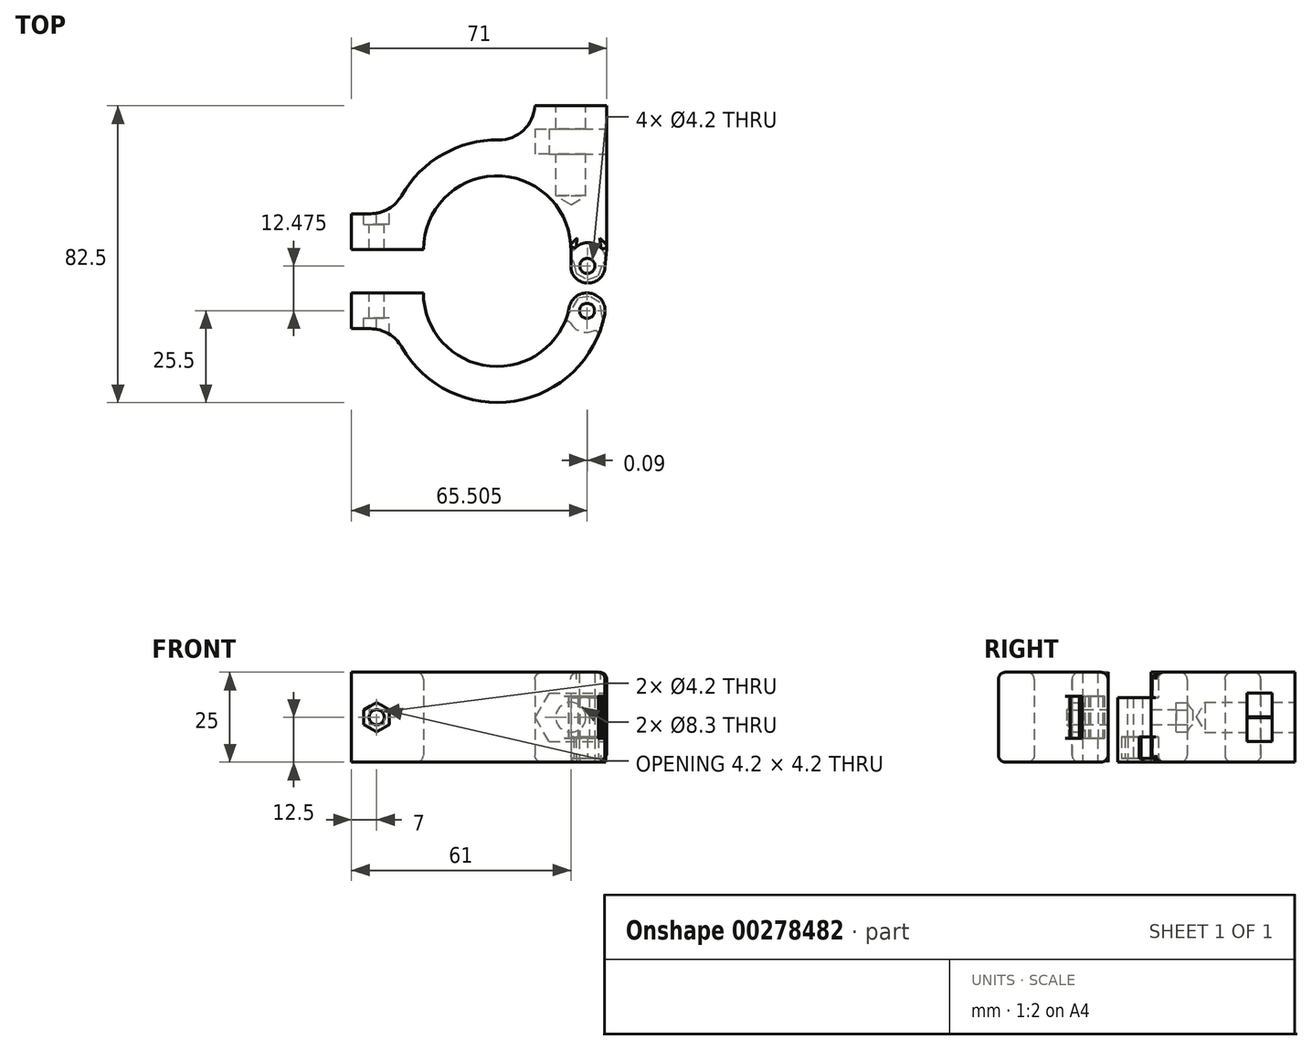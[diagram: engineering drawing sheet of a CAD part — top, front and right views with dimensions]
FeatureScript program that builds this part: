
annotation { "Feature Type Name" : "Feature", "Feature Type Description" : "" }
export const myFeature = defineFeature(function(context is Context, id is Id, definition is map)
    precondition{}
    {
        {
            var Q0;
            Q0=qCreatedBy(makeId("Top.planeOp"),FACE);
            var sketch = newSketch(context, id + "F0", { "sketchPlane" : qUnion([Q0])});
            skArc(sketch, "E0", {"start": v(20.5, 0) * mm, "mid": v(0, 20.5) * mm, "end": v(-20.5, 0) * mm});
            skArc(sketch, "E1", {"start": v(-28.81, 10) * mm, "mid": v(5.07, 30.08) * mm, "end": v(30.5, 0) * mm});
            skLineSegment(sketch, "E2", {"start": v(-30.5, 0) * mm, "end": v(-20.5, 0) * mm});
            skLineSegment(sketch, "E3", {"start": v(20.5, 0) * mm, "end": v(20.5, -5) * mm});
            skLineSegment(sketch, "E4", {"start": v(30, -5) * mm, "end": v(30.5, 0) * mm});
            skPoint(sketch, "E5", {"position": v(0, -12) * mm});
            skArc(sketch, "E6", {"start": v(20.5, -5) * mm, "mid": v(25.25, -9.3) * mm, "end": v(30, -5) * mm});
            skArc(sketch, "E7", {"start": v(-20.5, -12) * mm, "mid": v(-2.02, -32.4) * mm, "end": v(20.1, -16.02) * mm});
            skArc(sketch, "E8", {"start": v(-28.81, -22) * mm, "mid": v(2.08, -42.43) * mm, "end": v(29.9, -17.98) * mm});
            skLineSegment(sketch, "E9", {"start": v(25, -12) * mm, "end": v(25, -12) * mm});
            skLineSegment(sketch, "E10", {"start": v(-20.5, -12) * mm, "end": v(-30.5, -12) * mm});
            skPoint(sketch, "E11.visualSharp", {"position": v(20.5, -12) * mm});
            skArc(sketch, "E11.filletArc", {"start": v(25, -12) * mm, "mid": v(21.83, -13.13) * mm, "end": v(20.1, -16.02) * mm});
            skPoint(sketch, "E12.visualSharp", {"position": v(30.5, -12) * mm});
            skArc(sketch, "E12.filletArc", {"start": v(29.9, -17.98) * mm, "mid": v(28.87, -13.83) * mm, "end": v(25, -12) * mm});
            skCircle(sketch, "E13", {"center": v(25, -17) * mm, "radius": 2.1 * mm});
            skArc(sketch, "E14", {"start": v(19.88, -17.02) * mm, "mid": v(23.81, -22.9) * mm, "end": v(29.7, -18.96) * mm});
            skPoint(sketch, "E15", {"position": v(-25.5, 0) * mm});
            skArc(sketch, "E16", {"start": v(19.74, -16.14) * mm, "mid": v(-19.53, 16.4) * mm, "end": v(19.32, -16.65) * mm, "construction": true});
            skCircle(sketch, "E17", {"center": v(25.1, -4.52) * mm, "radius": 2.1 * mm});
            skArc(sketch, "E18", {"start": v(30.25, -2.5) * mm, "mid": v(25.64, 1.95) * mm, "end": v(20.5, -1.88) * mm});
            skLineSegment(sketch, "E19", {"start": v(-30.5, 0) * mm, "end": v(-40.5, 0) * mm});
            skLineSegment(sketch, "E20", {"start": v(-40.5, 0) * mm, "end": v(-40.5, 10) * mm});
            skLineSegment(sketch, "E21", {"start": v(-40.5, 10) * mm, "end": v(-28.81, 10) * mm});
            skLineSegment(sketch, "E22", {"start": v(-30.5, -12) * mm, "end": v(-40.5, -12) * mm});
            skLineSegment(sketch, "E23", {"start": v(-40.5, -12) * mm, "end": v(-40.5, -22) * mm});
            skLineSegment(sketch, "E24", {"start": v(-40.5, -22) * mm, "end": v(-28.81, -22) * mm});
            skLineSegment(sketch, "E25", {"start": v(30.5, 0) * mm, "end": v(30.5, 40) * mm});
            skLineSegment(sketch, "E26", {"start": v(30.5, 40) * mm, "end": v(10.5, 40) * mm});
            skLineSegment(sketch, "E27", {"start": v(10.5, 40) * mm, "end": v(10.5, 17.6) * mm});
            skArc(sketch, "E28", {"start": v(29.13, -18.41) * mm, "mid": v(29.22, -18.91) * mm, "end": v(29.64, -19.2) * mm});
            skArc(sketch, "E29", {"start": v(19.79, -17.36) * mm, "mid": v(20.27, -17.28) * mm, "end": v(20.56, -16.89) * mm});
            skArc(sketch, "E30", {"start": v(30.16, -3.4) * mm, "mid": v(29.76, -3.5) * mm, "end": v(29.5, -3.8) * mm});
            skArc(sketch, "E31", {"start": v(21.32, -3.62) * mm, "mid": v(21.08, -3.03) * mm, "end": v(20.5, -2.8) * mm});
            skLineSegment(sketch, "E32", {"start": v(21.92, -6.53) * mm, "end": v(25.16, -8.35) * mm});
            skLineSegment(sketch, "E33", {"start": v(25.16, -8.35) * mm, "end": v(28.18, -7.26) * mm});
            skLineSegment(sketch, "E34", {"start": v(28.18, -7.26) * mm, "end": v(29.5, -3.8) * mm});
            skPoint(sketch, "E35.center.orphan", {"position": v(25.25, -9.3) * mm});
            skPoint(sketch, "E36.start.orphan", {"position": v(21.32, -3.62) * mm});
            skLineSegment(sketch, "E37", {"start": v(21.32, -3.62) * mm, "end": v(21.92, -6.53) * mm});
            skLineSegment(sketch, "E38", {"start": v(20.56, -16.89) * mm, "end": v(22.42, -13.53) * mm});
            skLineSegment(sketch, "E39", {"start": v(22.42, -13.53) * mm, "end": v(25.66, -13.05) * mm});
            skPoint(sketch, "E39.endSnap0", {"position": v(25.66, -13) * mm});
            skLineSegment(sketch, "E40", {"start": v(25.66, -13.05) * mm, "end": v(28.58, -14.72) * mm});
            skLineSegment(sketch, "E41", {"start": v(28.58, -14.72) * mm, "end": v(29.13, -18.41) * mm});
            skSolve(sketch);
        }
        {
            var Q0;
            {var subQ1=sQuery(id+"F0.wireOp",EDGE,"E0");Q0=makeQuery(id+"F0.imprint","IMPRINT",FACE,{"disambiguationData":[TD([[makeQuery(id+"F0.imprint","IMPRINT",EDGE,{"derivedFrom":subQ1}),-1.0]])]});}
            var Q1;
            {var subQ6=sQuery(id+"F0.wireOp",EDGE,"E10");Q1=makeQuery(id+"F0.imprint","IMPRINT",FACE,{"disambiguationData":[TD([[makeQuery(id+"F0.imprint","IMPRINT",EDGE,{"derivedFrom":subQ6}),1.0]])]});}
            var Q2;
            {var subQ0=sQuery(id+"F0.wireOp",EDGE,"E25");Q2=makeQuery(id+"F0.imprint","IMPRINT",FACE,{"disambiguationData":[TD([[makeQuery(id+"F0.imprint","IMPRINT",EDGE,{"derivedFrom":subQ0}),1.0]])]});}
            var Q3;
            {var subQ0=sQuery(id+"F0.wireOp",EDGE,"E2");Q3=makeQuery(id+"F0.imprint","IMPRINT",FACE,{"disambiguationData":[TD([[makeQuery(id+"F0.imprint","IMPRINT",EDGE,{"derivedFrom":subQ0}),1.0]])]});}
            var Q4;
            {var subQ0=sQuery(id+"F0.wireOp",EDGE,"E14");var subQ1=sQuery(id+"F0.wireOp",EDGE,"E7");var subQ2=makeQuery(id+"F0.imprint","INTERSECT",VERTEX,{"derivedFrom":[subQ1,subQ0]});Q4=makeQuery(id+"F0.imprint","IMPRINT",FACE,{"disambiguationData":[TD([[makeQuery(id+"F0.imprint","IMPRINT",EDGE,{"disambiguationData":[TD([[subQ2,1.0]])],"derivedFrom":subQ1}),-1.0]])]});}
            extrude(context, id + "F1", {"entities" : qUnion([Q0, Q1, Q2, Q3, Q4]), "depth" : 25 * mm});
        }
        {
            var Q0;
            {var subQ0=sQuery(id+"F0.wireOp",EDGE,"E6");Q0=makeQuery(id+"F0.imprint","IMPRINT",FACE,{"disambiguationData":[TD([[makeQuery(id+"F0.imprint","IMPRINT",EDGE,{"derivedFrom":subQ0}),1.0]])]});}
            var Q1;
            {var subQ0=sQuery(id+"F0.wireOp",EDGE,"E35");var subQ1=sQuery(id+"F0.wireOp",EDGE,"E6");var subQ2=makeQuery(id+"F0.imprint","INTERSECT",VERTEX,{"disambiguationData":[OD(0.0)],"derivedFrom":[subQ1,subQ0]});Q1=makeQuery(id+"F0.imprint","IMPRINT",FACE,{"disambiguationData":[TD([[makeQuery(id+"F0.imprint","IMPRINT",EDGE,{"disambiguationData":[TD([[subQ2,-1.0]])],"derivedFrom":subQ1}),1.0]])]});}
            var Q2;
            {var subQ0=sQuery(id+"F0.wireOp",EDGE,"jxJWhOyt-H9XI-TiTa-gCL7-cOyN3CCPrfDy");var subQ1=sQuery(id+"F0.wireOp",EDGE,"E6");var subQ2=makeQuery(id+"F0.imprint","INTERSECT",VERTEX,{"disambiguationData":[OD(0.0)],"derivedFrom":[subQ1,subQ0]});Q2=makeQuery(id+"F0.imprint","IMPRINT",FACE,{"disambiguationData":[TD([[makeQuery(id+"F0.imprint","IMPRINT",EDGE,{"disambiguationData":[TD([[subQ2,-1.0]])],"derivedFrom":subQ1}),1.0]])]});}
            var Q3;
            {var subQ0=sQuery(id+"F0.wireOp",EDGE,"8LRzmeCb-BIhQ-DYdr-IcR4-9TPCuBTbz9Ep");var subQ1=sQuery(id+"F0.wireOp",EDGE,"E6");var subQ2=makeQuery(id+"F0.imprint","INTERSECT",VERTEX,{"disambiguationData":[OD(0.0)],"derivedFrom":[subQ1,subQ0]});Q3=makeQuery(id+"F0.imprint","IMPRINT",FACE,{"disambiguationData":[TD([[makeQuery(id+"F0.imprint","IMPRINT",EDGE,{"disambiguationData":[TD([[subQ2,-1.0]])],"derivedFrom":subQ1}),1.0]])]});}
            var Q4;
            {var subQ0=sQuery(id+"F0.wireOp",EDGE,"E31");var subQ1=sQuery(id+"F0.wireOp",EDGE,"E3");var subQ2=makeQuery(id+"F0.imprint","INTERSECT",VERTEX,{"disambiguationData":[OD(0.0)],"derivedFrom":[subQ1,subQ0]});Q4=makeQuery(id+"F0.imprint","IMPRINT",FACE,{"disambiguationData":[TD([[makeQuery(id+"F0.imprint","IMPRINT",EDGE,{"disambiguationData":[TD([[subQ2,-1.0]])],"derivedFrom":subQ1}),1.0]])]});}
            var Q5;
            {var subQ0=sQuery(id+"F0.wireOp",EDGE,"E30");var subQ1=sQuery(id+"F0.wireOp",EDGE,"E4");var subQ2=makeQuery(id+"F0.imprint","INTERSECT",VERTEX,{"disambiguationData":[OD(0.0)],"derivedFrom":[subQ1,subQ0]});Q5=makeQuery(id+"F0.imprint","IMPRINT",FACE,{"disambiguationData":[TD([[makeQuery(id+"F0.imprint","IMPRINT",EDGE,{"disambiguationData":[TD([[subQ2,-1.0]])],"derivedFrom":subQ1}),1.0]])]});}
            extrude(context, id + "F2", {"entities" : qUnion([Q0, Q1, Q2, Q3, Q4, Q5]), "operationType" : NewBodyOperationType.ADD, "depth" : 18 * mm, "hasSecondDirection" : true, "secondDirectionOppositeDirection" : false, "secondDirectionDepth" : 7 * mm});
        }
        {
            var Q0;
            {var subQ5=sQuery(id+"F0.wireOp",EDGE,"E11.filletArc");Q0=makeQuery(id+"F0.imprint","IMPRINT",FACE,{"disambiguationData":[TD([[makeQuery(id+"F0.imprint","IMPRINT",EDGE,{"derivedFrom":subQ5}),1.0]])]});}
            var Q1;
            Q1=makeQuery(id+"F0.imprint","IMPRINT",FACE,{"disambiguationData":[TD([[makeQuery(id+"F0.imprint","IMPRINT",EDGE,{"derivedFrom":sQuery(id+"F0.wireOp",EDGE,"E13")}),-1.0]])]});
            var Q2;
            {var subQ0=sQuery(id+"F0.wireOp",EDGE,"E12.filletArc");var subQ1=sQuery(id+"F0.wireOp",EDGE,"E11.filletArc");var subQ2=makeQuery(id+"F0.imprint","INTERSECT",VERTEX,{"derivedFrom":[subQ1,subQ0]});Q2=makeQuery(id+"F0.imprint","IMPRINT",FACE,{"disambiguationData":[TD([[makeQuery(id+"F0.imprint","IMPRINT",EDGE,{"disambiguationData":[TD([[subQ2,-1.0]])],"derivedFrom":subQ1}),1.0]])]});}
            var Q3;
            {var subQ0=sQuery(id+"F0.wireOp",EDGE,"uIjLM5ln-C2pQ-Ehxs-1cjr-M9Mzx9JWShuk");var subQ1=sQuery(id+"F0.wireOp",EDGE,"E12.filletArc");var subQ2=makeQuery(id+"F0.imprint","INTERSECT",VERTEX,{"disambiguationData":[OD(0.0)],"derivedFrom":[subQ1,subQ0]});Q3=makeQuery(id+"F0.imprint","IMPRINT",FACE,{"disambiguationData":[TD([[makeQuery(id+"F0.imprint","IMPRINT",EDGE,{"disambiguationData":[TD([[subQ2,-1.0]])],"derivedFrom":subQ1}),1.0]])]});}
            var Q4;
            {var subQ0=sQuery(id+"F0.wireOp",EDGE,"E14");var subQ1=sQuery(id+"F0.wireOp",EDGE,"E7");var subQ2=makeQuery(id+"F0.imprint","INTERSECT",VERTEX,{"derivedFrom":[subQ1,subQ0]});Q4=makeQuery(id+"F0.imprint","IMPRINT",FACE,{"disambiguationData":[TD([[makeQuery(id+"F0.imprint","IMPRINT",EDGE,{"disambiguationData":[TD([[subQ2,-1.0]])],"derivedFrom":subQ1}),-1.0]])]});}
            var Q5;
            {var subQ0=sQuery(id+"F0.wireOp",EDGE,"E8");var subQ1=makeQuery(id+"F0.imprint","INTERSECT",VERTEX,{"disambiguationData":[OD(0.0)],"derivedFrom":[subQ0,sQuery(id+"F0.wireOp",EDGE,"E14")]});Q5=makeQuery(id+"F0.imprint","IMPRINT",FACE,{"disambiguationData":[TD([[makeQuery(id+"F0.imprint","IMPRINT",EDGE,{"disambiguationData":[TD([[subQ1,1.0]])],"derivedFrom":subQ0}),1.0]])]});}
            extrude(context, id + "F3", {"entities" : qUnion([Q0, Q1, Q2, Q3, Q4, Q5]), "operationType" : NewBodyOperationType.ADD, "depth" : 6.7 * mm});
        }
        {
            var Q0;
            {var subQ0=sQuery(id+"F0.wireOp",EDGE,"E12.filletArc");var subQ1=sQuery(id+"F0.wireOp",EDGE,"E11.filletArc");var subQ2=makeQuery(id+"F0.imprint","INTERSECT",VERTEX,{"derivedFrom":[subQ1,subQ0]});Q0=makeQuery(id+"F0.imprint","IMPRINT",FACE,{"disambiguationData":[TD([[makeQuery(id+"F0.imprint","IMPRINT",EDGE,{"disambiguationData":[TD([[subQ2,-1.0]])],"derivedFrom":subQ1}),1.0]])]});}
            var Q1;
            {var subQ0=sQuery(id+"F0.wireOp",EDGE,"uIjLM5ln-C2pQ-Ehxs-1cjr-M9Mzx9JWShuk");var subQ1=sQuery(id+"F0.wireOp",EDGE,"E12.filletArc");var subQ2=makeQuery(id+"F0.imprint","INTERSECT",VERTEX,{"disambiguationData":[OD(0.0)],"derivedFrom":[subQ1,subQ0]});Q1=makeQuery(id+"F0.imprint","IMPRINT",FACE,{"disambiguationData":[TD([[makeQuery(id+"F0.imprint","IMPRINT",EDGE,{"disambiguationData":[TD([[subQ2,-1.0]])],"derivedFrom":subQ1}),1.0]])]});}
            var Q2;
            Q2=makeQuery(id+"F0.imprint","IMPRINT",FACE,{"disambiguationData":[TD([[makeQuery(id+"F0.imprint","IMPRINT",EDGE,{"derivedFrom":sQuery(id+"F0.wireOp",EDGE,"E13")}),-1.0]])]});
            var Q3;
            {var subQ0=sQuery(id+"F0.wireOp",EDGE,"kNw9iPZq-PIQ4-ABiH-hurB-JV7T6kJgDTR0");var subQ1=sQuery(id+"F0.wireOp",EDGE,"E11.filletArc");var subQ2=makeQuery(id+"F0.imprint","INTERSECT",VERTEX,{"disambiguationData":[OD(0.0)],"derivedFrom":[subQ1,subQ0]});Q3=makeQuery(id+"F0.imprint","IMPRINT",FACE,{"disambiguationData":[TD([[makeQuery(id+"F0.imprint","IMPRINT",EDGE,{"disambiguationData":[TD([[subQ2,-1.0]])],"derivedFrom":subQ1}),1.0]])]});}
            var Q4;
            {var subQ0=sQuery(id+"F0.wireOp",EDGE,"E14");var subQ1=sQuery(id+"F0.wireOp",EDGE,"E7");var subQ2=makeQuery(id+"F0.imprint","INTERSECT",VERTEX,{"derivedFrom":[subQ1,subQ0]});Q4=makeQuery(id+"F0.imprint","IMPRINT",FACE,{"disambiguationData":[TD([[makeQuery(id+"F0.imprint","IMPRINT",EDGE,{"disambiguationData":[TD([[subQ2,-1.0]])],"derivedFrom":subQ1}),-1.0]])]});}
            var Q5;
            {var subQ0=sQuery(id+"F0.wireOp",EDGE,"E8");var subQ1=makeQuery(id+"F0.imprint","INTERSECT",VERTEX,{"disambiguationData":[OD(0.0)],"derivedFrom":[subQ0,sQuery(id+"F0.wireOp",EDGE,"E14")]});Q5=makeQuery(id+"F0.imprint","IMPRINT",FACE,{"disambiguationData":[TD([[makeQuery(id+"F0.imprint","IMPRINT",EDGE,{"disambiguationData":[TD([[subQ1,1.0]])],"derivedFrom":subQ0}),1.0]])]});}
            extrude(context, id + "F4", {"entities" : qUnion([Q0, Q1, Q2, Q3, Q4, Q5]), "operationType" : NewBodyOperationType.ADD, "depth" : 25 * mm, "hasSecondDirection" : true, "secondDirectionOppositeDirection" : false, "secondDirectionDepth" : 18.3 * mm});
        }
        {
            var Q0;
            Q0=makeQuery(id+"F1.opExtrude","SWEPT_EDGE",EDGE,{"disambiguationData":[OSD([sQuery(id+"F0.wireOp",EDGE,"E8"),sQuery(id+"F0.wireOp",EDGE,"E14")])]});
            var Q1;
            {var subQ0=sQuery(id+"F0.wireOp",EDGE,"E18");var subQ1=sQuery(id+"F0.wireOp",EDGE,"E4");var subQ2=sQuery(id+"F0.wireOp",EDGE,"E3");Q1=makeQuery(id+"F2.boolean.opBoolean","SPLIT",EDGE,{"disambiguationData":[TD([makeQuery(id+"F2.opExtrude","CAP_FACE",FACE,{"disambiguationData":[OSD([subQ2,subQ1,sQuery(id+"F0.wireOp",EDGE,"E6"),sQuery(id+"F0.wireOp",EDGE,"E17"),subQ0])],"isStart":true})])],"derivedFrom":makeQuery(id+"F1.opExtrude","SWEPT_EDGE",EDGE,{"disambiguationData":[OSD([subQ1,subQ0])]})});}
            var Q2;
            {var subQ0=sQuery(id+"F0.wireOp",EDGE,"E18");var subQ1=sQuery(id+"F0.wireOp",EDGE,"E4");var subQ2=sQuery(id+"F0.wireOp",EDGE,"E3");Q2=makeQuery(id+"F2.boolean.opBoolean","SPLIT",EDGE,{"disambiguationData":[TD([makeQuery(id+"F2.opExtrude","CAP_FACE",FACE,{"disambiguationData":[OSD([subQ2,subQ1,sQuery(id+"F0.wireOp",EDGE,"E6"),sQuery(id+"F0.wireOp",EDGE,"E17"),subQ0])],"isStart":false})])],"derivedFrom":makeQuery(id+"F1.opExtrude","SWEPT_EDGE",EDGE,{"disambiguationData":[OSD([subQ1,subQ0])]})});}
            var Q3;
            {var subQ0=sQuery(id+"F0.wireOp",EDGE,"E3");var subQ1=sQuery(id+"F0.wireOp",EDGE,"E18");var subQ2=sQuery(id+"F0.wireOp",EDGE,"E4");Q3=makeQuery(id+"F2.boolean.opBoolean","SPLIT",EDGE,{"disambiguationData":[TD([makeQuery(id+"F2.opExtrude","CAP_FACE",FACE,{"disambiguationData":[OSD([subQ0,subQ2,sQuery(id+"F0.wireOp",EDGE,"E6"),sQuery(id+"F0.wireOp",EDGE,"E17"),subQ1])],"isStart":false})])],"derivedFrom":makeQuery(id+"F1.opExtrude","SWEPT_EDGE",EDGE,{"disambiguationData":[OSD([subQ0,subQ1])]})});}
            var Q4;
            {var subQ0=sQuery(id+"F0.wireOp",EDGE,"E18");var subQ1=sQuery(id+"F0.wireOp",EDGE,"E3");var subQ2=sQuery(id+"F0.wireOp",EDGE,"E4");Q4=makeQuery(id+"F2.boolean.opBoolean","SPLIT",EDGE,{"disambiguationData":[TD([makeQuery(id+"F2.opExtrude","CAP_FACE",FACE,{"disambiguationData":[OSD([subQ1,subQ2,sQuery(id+"F0.wireOp",EDGE,"E6"),sQuery(id+"F0.wireOp",EDGE,"E17"),subQ0])],"isStart":true})])],"derivedFrom":makeQuery(id+"F1.opExtrude","SWEPT_EDGE",EDGE,{"disambiguationData":[OSD([subQ1,subQ0])]})});}
            var Q5;
            {var subQ0=sQuery(id+"F0.wireOp",EDGE,"E14");var subQ1=makeQuery(id+"F1.opExtrude","SWEPT_FACE",FACE,{"disambiguationData":[OSD([subQ0])]});var subQ2=sQuery(id+"F0.wireOp",EDGE,"E29");Q5=makeQuery(id+"F4.boolean.opBoolean","SPLIT",EDGE,{"disambiguationData":[topologyDisambiguationEdgeConnected([subQ1])],"derivedFrom":makeQuery(id+"F3.boolean.opBoolean","SPLIT",EDGE,{"disambiguationData":[topologyDisambiguationEdgeConnected([subQ1])],"derivedFrom":makeQuery(id+"F1.opExtrude","SWEPT_EDGE",EDGE,{"disambiguationData":[OSD([subQ0,subQ2])]})})});}
            fillet(context, id + "F5", {"entities" : qUnion([Q0, Q1, Q2, Q3, Q4, Q5]), "radius" : 1 * mm, "tangentPropagation" : true, "allowEdgeOverflow" : false});
        }
        {
            var Q0;
            Q0=makeQuery(id+"F1.opExtrude","SWEPT_EDGE",EDGE,{"disambiguationData":[OSD([sQuery(id+"F0.wireOp",EDGE,"E1"),sQuery(id+"F0.wireOp",EDGE,"E21")])]});
            var Q1;
            Q1=makeQuery(id+"F1.opExtrude","SWEPT_EDGE",EDGE,{"disambiguationData":[OSD([sQuery(id+"F0.wireOp",EDGE,"E1"),sQuery(id+"F0.wireOp",EDGE,"E27")])]});
            var Q2;
            Q2=makeQuery(id+"F1.opExtrude","SWEPT_EDGE",EDGE,{"disambiguationData":[OSD([sQuery(id+"F0.wireOp",EDGE,"E8"),sQuery(id+"F0.wireOp",EDGE,"E24")])]});
            var Q3;
            {var subQ0=sQuery(id+"F0.wireOp",EDGE,"E14");var subQ1=makeQuery(id+"F1.opExtrude","SWEPT_FACE",FACE,{"disambiguationData":[OSD([subQ0])]});var subQ2=sQuery(id+"F0.wireOp",EDGE,"E29");Q3=makeQuery(id+"F5.opFillet","BLEND_EDGE",EDGE,{"blendedFrom":[makeQuery(id+"F4.boolean.opBoolean","SPLIT",EDGE,{"disambiguationData":[topologyDisambiguationEdgeConnected([subQ1])],"derivedFrom":makeQuery(id+"F3.boolean.opBoolean","SPLIT",EDGE,{"disambiguationData":[topologyDisambiguationEdgeConnected([subQ1])],"derivedFrom":makeQuery(id+"F1.opExtrude","SWEPT_EDGE",EDGE,{"disambiguationData":[OSD([subQ0,subQ2])]})})}),makeQuery(id+"F1.opExtrude","SWEPT_FACE",FACE,{"disambiguationData":[OSD([sQuery(id+"F0.wireOp",EDGE,"E7")])]})],"blendedInto":[makeQuery(id+"F1.opExtrude","SWEPT_FACE",FACE,{"disambiguationData":[OSD([sQuery(id+"F0.wireOp",EDGE,"E7")])]})]});}
            fillet(context, id + "F6", {"entities" : qUnion([Q0, Q1, Q2, Q3]), "radius" : 10 * mm, "tangentPropagation" : true, "allowEdgeOverflow" : false});
        }
        {
            var Q0;
            Q0=makeQuery(id+"F1.opExtrude","SWEPT_FACE",FACE,{"disambiguationData":[OSD([sQuery(id+"F0.wireOp",EDGE,"E21")])]});
            var sketch = newSketch(context, id + "F7", { "sketchPlane" : qUnion([Q0])});
            skCircle(sketch, "E42", {"center": v(33.5, 12.5) * mm, "radius": 2.1 * mm});
            skPoint(sketch, "E42.centerSnap0", {"position": v(35.22, 12.5) * mm});
            skCircle(sketch, "E43.cCircle", {"center": v(33.5, 12.5) * mm, "radius": 3.55 * mm, "construction": true});
            skPoint(sketch, "E43.cCircle.perimeterSnap0", {"position": v(40.5, 12.5) * mm});
            skLineSegment(sketch, "E43.0", {"start": v(37.05, 14.55) * mm, "end": v(37.05, 10.45) * mm});
            skLineSegment(sketch, "E43.1", {"start": v(37.05, 10.45) * mm, "end": v(33.5, 8.4) * mm});
            skLineSegment(sketch, "E43.2", {"start": v(33.5, 8.4) * mm, "end": v(29.95, 10.45) * mm});
            skLineSegment(sketch, "E43.3", {"start": v(29.95, 10.45) * mm, "end": v(29.95, 14.55) * mm});
            skLineSegment(sketch, "E43.4", {"start": v(29.95, 14.55) * mm, "end": v(33.5, 16.6) * mm});
            skLineSegment(sketch, "E43.5", {"start": v(33.5, 16.6) * mm, "end": v(37.05, 14.55) * mm});
            skPoint(sketch, "E43.0.midPoint", {"position": v(37.05, 12.5) * mm});
            skPoint(sketch, "E43.0.midPoint.positionSnap0", {"position": v(40.5, 12.5) * mm});
            skSolve(sketch);
        }
        {
            var Q0;
            {var subQ0=sQuery(id+"F7.wireOp",EDGE,"E42");var subQ1=sQuery(id+"F0.wireOp",EDGE,"E21");var subQ2=makeQuery(id+"F6.opFillet","BLEND_EDGE",EDGE,{"blendedFrom":[makeQuery(id+"F1.opExtrude","SWEPT_EDGE",EDGE,{"disambiguationData":[OSD([sQuery(id+"F0.wireOp",EDGE,"E1"),subQ1])]}),makeQuery(id+"F1.opExtrude","SWEPT_FACE",FACE,{"disambiguationData":[OSD([subQ1])]})],"blendedInto":[makeQuery(id+"F1.opExtrude","SWEPT_FACE",FACE,{"disambiguationData":[OSD([subQ1])]})]});var subQ3=makeQuery(id+"F7.imprint","INTERSECT",VERTEX,{"disambiguationData":[OD(0.0)],"derivedFrom":[subQ2,subQ0]});Q0=makeQuery(id+"F7.imprint","IMPRINT",FACE,{"disambiguationData":[TD([[makeQuery(id+"F7.imprint","IMPRINT",EDGE,{"disambiguationData":[TD([[subQ3,1.0]])],"derivedFrom":subQ0}),1.0]])]});}
            var Q1;
            {var subQ0=sQuery(id+"F7.wireOp",EDGE,"E42");var subQ1=sQuery(id+"F0.wireOp",EDGE,"E21");var subQ2=makeQuery(id+"F6.opFillet","BLEND_EDGE",EDGE,{"blendedFrom":[makeQuery(id+"F1.opExtrude","SWEPT_EDGE",EDGE,{"disambiguationData":[OSD([sQuery(id+"F0.wireOp",EDGE,"E1"),subQ1])]}),makeQuery(id+"F1.opExtrude","SWEPT_FACE",FACE,{"disambiguationData":[OSD([subQ1])]})],"blendedInto":[makeQuery(id+"F1.opExtrude","SWEPT_FACE",FACE,{"disambiguationData":[OSD([subQ1])]})]});var subQ3=makeQuery(id+"F7.imprint","INTERSECT",VERTEX,{"disambiguationData":[OD(0.0)],"derivedFrom":[subQ2,subQ0]});Q1=makeQuery(id+"F7.imprint","IMPRINT",FACE,{"disambiguationData":[TD([[makeQuery(id+"F7.imprint","IMPRINT",EDGE,{"disambiguationData":[TD([[subQ3,-1.0]])],"derivedFrom":subQ0}),1.0]])]});}
            extrude(context, id + "F8", {"entities" : qUnion([Q0, Q1]), "operationType" : NewBodyOperationType.REMOVE, "oppositeDirection" : true, "depth" : 40 * mm, "hasSecondDirection" : true, "secondDirectionOppositeDirection" : false, "secondDirectionDepth" : 25 * mm});
        }
        {
            var Q0;
            {var subQ1=sQuery(id+"F7.wireOp",EDGE,"E43.0");Q0=makeQuery(id+"F7.imprint","IMPRINT",FACE,{"disambiguationData":[TD([[makeQuery(id+"F7.imprint","IMPRINT",EDGE,{"derivedFrom":subQ1}),-1.0]])]});}
            var Q1;
            {var subQ0=sQuery(id+"F7.wireOp",EDGE,"E43.2");Q1=makeQuery(id+"F7.imprint","IMPRINT",FACE,{"disambiguationData":[TD([[makeQuery(id+"F7.imprint","IMPRINT",EDGE,{"derivedFrom":subQ0}),-1.0]])]});}
            extrude(context, id + "F9", {"entities" : qUnion([Q0, Q1]), "operationType" : NewBodyOperationType.REMOVE, "oppositeDirection" : true, "depth" : 3 * mm, "hasSecondDirection" : true, "secondDirectionOppositeDirection" : false, "secondDirectionDepth" : 25 * mm});
        }
        {
            var Q0;
            {var subQ1=sQuery(id+"F7.wireOp",EDGE,"E43.0");Q0=makeQuery(id+"F7.imprint","IMPRINT",FACE,{"disambiguationData":[TD([[makeQuery(id+"F7.imprint","IMPRINT",EDGE,{"derivedFrom":subQ1}),-1.0]])]});}
            var Q1;
            {var subQ0=sQuery(id+"F7.wireOp",EDGE,"E43.2");Q1=makeQuery(id+"F7.imprint","IMPRINT",FACE,{"disambiguationData":[TD([[makeQuery(id+"F7.imprint","IMPRINT",EDGE,{"derivedFrom":subQ0}),-1.0]])]});}
            extrude(context, id + "F10", {"entities" : qUnion([Q0, Q1]), "operationType" : NewBodyOperationType.REMOVE, "oppositeDirection" : true, "depth" : 50 * mm, "hasSecondDirection" : true, "secondDirectionOppositeDirection" : true, "secondDirectionDepth" : 29 * mm});
        }
        {
            var Q0;
            Q0=makeQuery(id+"F1.opExtrude","SWEPT_FACE",FACE,{"disambiguationData":[OSD([sQuery(id+"F0.wireOp",EDGE,"E26")])]});
            var sketch = newSketch(context, id + "F11", { "sketchPlane" : qUnion([Q0])});
            skPoint(sketch, "E44", {"position": v(-20.5, 12.5) * mm});
            skPoint(sketch, "E44.positionSnap0", {"position": v(-20.5, 0) * mm});
            skPoint(sketch, "E44.positionSnap1", {"position": v(-10.5, 12.5) * mm});
            skSolve(sketch);
        }
        {
            var Q0;
            Q0=makeQuery(id+"F1.opExtrude","SWEPT_FACE",FACE,{"disambiguationData":[OSD([sQuery(id+"F0.wireOp",EDGE,"E25")])]});
            var sketch = newSketch(context, id + "F12", { "sketchPlane" : qUnion([Q0])});
            skLineSegment(sketch, "E45.bottom", {"start": v(26.59, 5.75) * mm, "end": v(33.59, 5.75) * mm});
            skLineSegment(sketch, "E45.top", {"start": v(26.59, 19.25) * mm, "end": v(33.59, 19.25) * mm});
            skLineSegment(sketch, "E45.left", {"start": v(26.59, 5.75) * mm, "end": v(26.59, 19.25) * mm});
            skLineSegment(sketch, "E45.right", {"start": v(33.59, 5.75) * mm, "end": v(33.59, 19.25) * mm});
            skPoint(sketch, "E45.middle", {"position": v(30.09, 12.5) * mm});
            skPoint(sketch, "E45.middle.positionSnap0", {"position": v(40, 12.5) * mm});
            skPoint(sketch, "E45.centerSnap0", {"position": v(40, 12.5) * mm});
            skSolve(sketch);
        }
        {
            var Q0;
            Q0=makeQuery(id+"F12.imprint","IMPRINT",FACE,{"disambiguationData":[TD([[makeQuery(id+"F12.imprint","IMPRINT",EDGE,{"derivedFrom":sQuery(id+"F12.wireOp",EDGE,"E45.bottom")}),1.0]])]});
            extrude(context, id + "F13", {"entities" : qUnion([Q0]), "operationType" : NewBodyOperationType.REMOVE, "oppositeDirection" : true, "depth" : 19.8 * mm});
        }
        {
            var Q0;
            Q0=sQuery(id+"F11.wireOp",VERTEX,"E44");
            var Q1;
            Q1=makeQuery(id+"F1.opExtrude","SWEPT_BODY",BODY,{"disambiguationData":[OSD([sQuery(id+"F0.wireOp",EDGE,"E0"),sQuery(id+"F0.wireOp",EDGE,"E1"),sQuery(id+"F0.wireOp",EDGE,"E2"),sQuery(id+"F0.wireOp",EDGE,"E3"),sQuery(id+"F0.wireOp",EDGE,"E4"),sQuery(id+"F0.wireOp",EDGE,"E18"),sQuery(id+"F0.wireOp",EDGE,"E19"),sQuery(id+"F0.wireOp",EDGE,"E20"),sQuery(id+"F0.wireOp",EDGE,"E21"),sQuery(id+"F0.wireOp",EDGE,"E25"),sQuery(id+"F0.wireOp",EDGE,"E26"),sQuery(id+"F0.wireOp",EDGE,"E27")])]});
            hole(context, id + "F14", {"style" : HoleStyle.SIMPLE, "endStyle" : HoleEndStyle.BLIND, "holeDiameter" : 8.3 * mm, "holeDepth" : 25 * mm, "tappedDepth" : 12 * mm, "tapClearance" : 3, "startFromSketch" : true, "locations" : qUnion([Q0]), "scope" : qUnion([Q1])});
        }
        {
            var Q0;
            Q0=makeQuery(id+"F13.boolean.opBoolean","COPY",EDGE,{"derivedFrom":makeQuery(id+"F13.opExtrude","CAP_EDGE",EDGE,{"disambiguationData":[OSD([sQuery(id+"F12.wireOp",EDGE,"E45.top")])],"isStart":false})});
            var Q1;
            Q1=makeQuery(id+"F13.boolean.opBoolean","COPY",EDGE,{"derivedFrom":makeQuery(id+"F13.opExtrude","CAP_EDGE",EDGE,{"disambiguationData":[OSD([sQuery(id+"F12.wireOp",EDGE,"E45.bottom")])],"isStart":false})});
            chamfer(context, id + "F15", {"entities" : qUnion([Q0, Q1]), "chamferType" : ChamferType.OFFSET_ANGLE, "width" : 3.8 * mm, "oppositeDirection" : false, "angle" : 60 * degree, "tangentPropagation" : true});
        }
        {
            var Q0;
            {var subQ0=sQuery(id+"F0.wireOp",EDGE,"E8");Q0=makeQuery(id+"F3.boolean.opBoolean","MERGE",EDGE,{"derivedFrom":[makeQuery(id+"F1.opExtrude","CAP_EDGE",EDGE,{"disambiguationData":[OSD([subQ0])],"isStart":true}),makeQuery(id+"F3.opExtrude","CAP_EDGE",EDGE,{"disambiguationData":[OSD([subQ0])],"isStart":true})]});}
            var Q1;
            {var subQ0=sQuery(id+"F0.wireOp",EDGE,"E8");Q1=makeQuery(id+"F4.boolean.opBoolean","MERGE",EDGE,{"derivedFrom":[makeQuery(id+"F1.opExtrude","CAP_EDGE",EDGE,{"disambiguationData":[OSD([subQ0])],"isStart":false}),makeQuery(id+"F4.opExtrude","CAP_EDGE",EDGE,{"disambiguationData":[OSD([subQ0])],"isStart":false})]});}
            var Q2;
            Q2=makeQuery(id+"F1.opExtrude","CAP_EDGE",EDGE,{"disambiguationData":[OSD([sQuery(id+"F0.wireOp",EDGE,"E0")])],"isStart":false});
            var Q3;
            Q3=makeQuery(id+"F1.opExtrude","CAP_EDGE",EDGE,{"disambiguationData":[OSD([sQuery(id+"F0.wireOp",EDGE,"E1")])],"isStart":false});
            var Q4;
            Q4=makeQuery(id+"F1.opExtrude","CAP_EDGE",EDGE,{"disambiguationData":[OSD([sQuery(id+"F0.wireOp",EDGE,"E1")])],"isStart":true});
            var Q5;
            Q5=makeQuery(id+"F1.opExtrude","CAP_EDGE",EDGE,{"disambiguationData":[OSD([sQuery(id+"F0.wireOp",EDGE,"E25")])],"isStart":true});
            fillet(context, id + "F16", {"entities" : qUnion([Q0, Q1, Q2, Q3, Q4, Q5]), "radius" : 2 * mm, "tangentPropagation" : true, "allowEdgeOverflow" : false});
        }
        {
            var Q0;
            {var subQ1=sQuery(id+"F0.wireOp",EDGE,"E6");Q0=makeQuery(id+"F0.imprint","IMPRINT",FACE,{"disambiguationData":[TD([[makeQuery(id+"F0.imprint","IMPRINT",EDGE,{"derivedFrom":subQ1}),1.0]])]});}
            extrude(context, id + "F17", {"entities" : qUnion([Q0]), "operationType" : NewBodyOperationType.ADD, "depth" : 7 * mm});
        }
        {
            var Q0;
            Q0=makeQuery(id+"F0.imprint","IMPRINT",FACE,{"disambiguationData":[TD([[makeQuery(id+"F0.imprint","IMPRINT",EDGE,{"derivedFrom":sQuery(id+"F0.wireOp",EDGE,"E17")}),-1.0]])]});
            extrude(context, id + "F18", {"entities" : qUnion([Q0]), "operationType" : NewBodyOperationType.ADD, "depth" : 1 * mm});
        }
        {
            var Q0;
            {var subQ0=sQuery(id+"F0.wireOp",EDGE,"E8");var subQ1=makeQuery(id+"F0.imprint","INTERSECT",VERTEX,{"disambiguationData":[OD(0.0)],"derivedFrom":[subQ0,sQuery(id+"F0.wireOp",EDGE,"E14")]});Q0=makeQuery(id+"F0.imprint","IMPRINT",FACE,{"disambiguationData":[TD([[makeQuery(id+"F0.imprint","IMPRINT",EDGE,{"disambiguationData":[TD([[subQ1,1.0]])],"derivedFrom":subQ0}),1.0]])]});}
            extrude(context, id + "F19", {"entities" : qUnion([Q0]), "operationType" : NewBodyOperationType.ADD, "depth" : 20 * mm, "hasSecondDirection" : true, "secondDirectionOppositeDirection" : false, "secondDirectionDepth" : 5 * mm});
        }
    });
